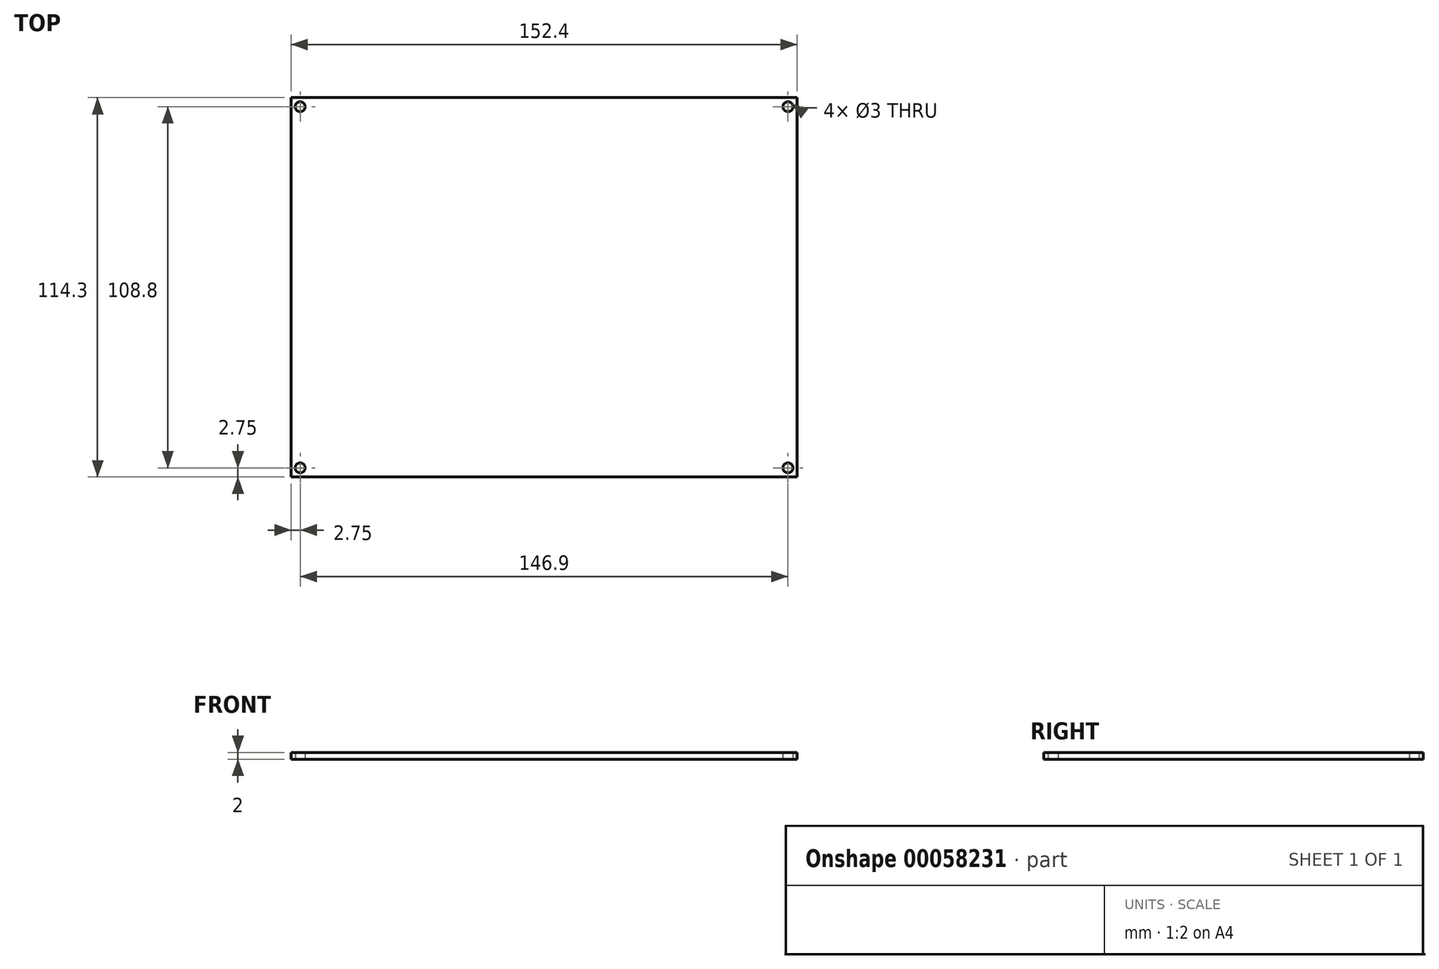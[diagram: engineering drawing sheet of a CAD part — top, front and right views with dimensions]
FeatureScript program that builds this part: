
annotation { "Feature Type Name" : "Feature", "Feature Type Description" : "" }
export const myFeature = defineFeature(function(context is Context, id is Id, definition is map)
    precondition{}
    {
        {
            var Q0;
            Q0=qCreatedBy(makeId("Top.planeOp"),FACE);
            var sketch = newSketch(context, id + "F0", { "sketchPlane" : qUnion([Q0])});
            skLineSegment(sketch, "E0.rect.bottom", {"start": v(76.2, 57.15) * mm, "end": v(-76.2, 57.15) * mm});
            skLineSegment(sketch, "E0.rect.top", {"start": v(76.2, -57.15) * mm, "end": v(-76.2, -57.15) * mm});
            skLineSegment(sketch, "E0.rect.left", {"start": v(76.2, 57.15) * mm, "end": v(76.2, -57.15) * mm});
            skLineSegment(sketch, "E0.rect.right", {"start": v(-76.2, 57.15) * mm, "end": v(-76.2, -57.15) * mm});
            skPoint(sketch, "E0.rect.middle", {"position": v(0, 0) * mm});
            skLineSegment(sketch, "E1", {"start": v(0, 57.15) * mm, "end": v(0, 0) * mm, "construction": true});
            skLineSegment(sketch, "E2", {"start": v(-76.2, 0) * mm, "end": v(0, 0) * mm, "construction": true});
            skCircle(sketch, "E3", {"center": v(-73.45, 54.4) * mm, "radius": 1.5 * mm});
            skCircle(sketch, "E4.MirrorC", {"center": v(73.45, 54.4) * mm, "radius": 1.5 * mm});
            skCircle(sketch, "E5.MirrorC", {"center": v(-73.45, -54.4) * mm, "radius": 1.5 * mm});
            skCircle(sketch, "E6.MirrorC", {"center": v(73.45, -54.4) * mm, "radius": 1.5 * mm});
            skSolve(sketch);
        }
        {
            var Q0;
            Q0 = qSketchRegion(id + "F0", true);
            extrude(context, id + "F1", {"entities" : qUnion([Q0]), "depth" : 2 * mm});
        }
    });
